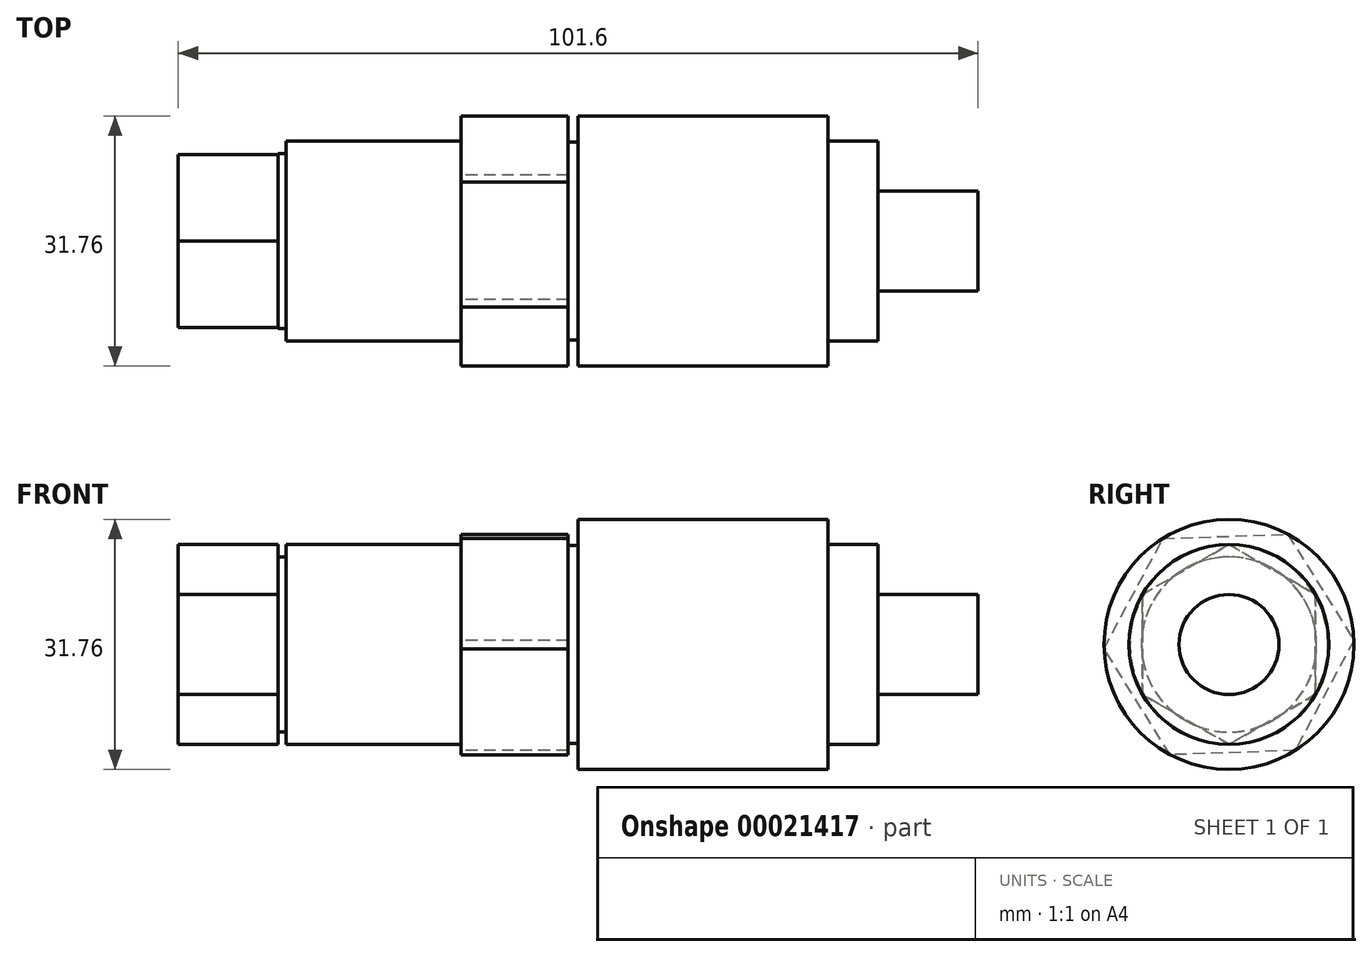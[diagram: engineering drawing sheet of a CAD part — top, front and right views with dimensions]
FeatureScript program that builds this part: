
annotation { "Feature Type Name" : "Feature", "Feature Type Description" : "" }
export const myFeature = defineFeature(function(context is Context, id is Id, definition is map)
    precondition{}
    {
        {
            var Q0;
            Q0=qCreatedBy(makeId("Front.planeOp"),FACE);
            var sketch = newSketch(context, id + "F0", { "sketchPlane" : qUnion([Q0])});
            skLineSegment(sketch, "E0", {"start": v(0, 0) * mm, "end": v(101.6, 0) * mm});
            skLineSegment(sketch, "E1", {"start": v(101.6, 0) * mm, "end": v(101.6, 6.35) * mm});
            skLineSegment(sketch, "E2", {"start": v(101.6, 6.35) * mm, "end": v(88.9, 6.35) * mm});
            skLineSegment(sketch, "E3", {"start": v(88.9, 6.35) * mm, "end": v(88.9, 12.7) * mm});
            skLineSegment(sketch, "E4", {"start": v(88.9, 12.7) * mm, "end": v(82.55, 12.7) * mm});
            skLineSegment(sketch, "E5", {"start": v(82.55, 12.7) * mm, "end": v(82.55, 15.88) * mm});
            skLineSegment(sketch, "E6", {"start": v(82.55, 15.88) * mm, "end": v(50.8, 15.87) * mm});
            skLineSegment(sketch, "E7", {"start": v(50.8, 15.87) * mm, "end": v(50.8, 12.57) * mm});
            skLineSegment(sketch, "E8", {"start": v(50.8, 12.57) * mm, "end": v(49.53, 12.57) * mm});
            skLineSegment(sketch, "E9", {"start": v(49.53, 12.57) * mm, "end": v(49.53, 15.88) * mm});
            skLineSegment(sketch, "E10", {"start": v(49.53, 15.88) * mm, "end": v(35.94, 15.87) * mm});
            skLineSegment(sketch, "E11", {"start": v(35.94, 15.87) * mm, "end": v(35.94, 12.7) * mm});
            skLineSegment(sketch, "E12", {"start": v(35.94, 12.7) * mm, "end": v(13.72, 12.7) * mm});
            skLineSegment(sketch, "E13", {"start": v(13.72, 12.7) * mm, "end": v(13.72, 11.13) * mm});
            skLineSegment(sketch, "E14", {"start": v(13.72, 11.13) * mm, "end": v(12.7, 11.13) * mm});
            skLineSegment(sketch, "E15", {"start": v(12.7, 11.13) * mm, "end": v(12.7, 12.7) * mm});
            skLineSegment(sketch, "E16", {"start": v(12.7, 12.7) * mm, "end": v(0, 12.7) * mm});
            skLineSegment(sketch, "E17", {"start": v(0, 12.7) * mm, "end": v(0, 0) * mm});
            skSolve(sketch);
        }
        {
            var Q0;
            Q0=makeQuery(id+"F0.imprint","IMPRINT",FACE,{"disambiguationData":[TD([[makeQuery(id+"F0.imprint","IMPRINT",EDGE,{"derivedFrom":sQuery(id+"F0.wireOp",EDGE,"E0")}),1.0]])]});
            var Q1;
            Q1=sQuery(id+"F0.wireOp",EDGE,"E0");
            revolve(context, id + "F1", {"entities" : qUnion([Q0]), "axis" : qUnion([Q1]), "revolveType" : RevolveType.FULL});
        }
        {
            var Q0;
            Q0=makeQuery(id+"F1.opRevolve","SWEPT_FACE",FACE,{"disambiguationData":[OSD([sQuery(id+"F0.wireOp",EDGE,"E17")])]});
            var sketch = newSketch(context, id + "F2", { "sketchPlane" : qUnion([Q0])});
            skCircle(sketch, "E18.cCircle", {"center": v(0, 0) * mm, "radius": 12.7 * mm, "construction": true});
            skLineSegment(sketch, "E18.0", {"start": v(0, 12.7) * mm, "end": v(11, 6.35) * mm});
            skLineSegment(sketch, "E18.1", {"start": v(11, 6.35) * mm, "end": v(11, -6.35) * mm});
            skLineSegment(sketch, "E18.2", {"start": v(11, -6.35) * mm, "end": v(0, -12.7) * mm});
            skLineSegment(sketch, "E18.3", {"start": v(0, -12.7) * mm, "end": v(-11, -6.35) * mm});
            skLineSegment(sketch, "E18.4", {"start": v(-11, -6.35) * mm, "end": v(-11, 6.35) * mm});
            skLineSegment(sketch, "E18.5", {"start": v(-11, 6.35) * mm, "end": v(0, 12.7) * mm});
            skSolve(sketch);
        }
        {
            var Q0;
            {var subQ1=sQuery(id+"F2.wireOp",EDGE,"E18.3");Q0=makeQuery(id+"F2.imprint","IMPRINT",FACE,{"disambiguationData":[TD([[makeQuery(id+"F2.imprint","IMPRINT",EDGE,{"derivedFrom":subQ1}),1.0]])]});}
            var Q1;
            {var subQ1=sQuery(id+"F2.wireOp",EDGE,"E18.4");Q1=makeQuery(id+"F2.imprint","IMPRINT",FACE,{"disambiguationData":[TD([[makeQuery(id+"F2.imprint","IMPRINT",EDGE,{"derivedFrom":subQ1}),1.0]])]});}
            var Q2;
            {var subQ1=sQuery(id+"F2.wireOp",EDGE,"E18.5");Q2=makeQuery(id+"F2.imprint","IMPRINT",FACE,{"disambiguationData":[TD([[makeQuery(id+"F2.imprint","IMPRINT",EDGE,{"derivedFrom":subQ1}),1.0]])]});}
            var Q3;
            {var subQ1=sQuery(id+"F2.wireOp",EDGE,"E18.0");Q3=makeQuery(id+"F2.imprint","IMPRINT",FACE,{"disambiguationData":[TD([[makeQuery(id+"F2.imprint","IMPRINT",EDGE,{"derivedFrom":subQ1}),1.0]])]});}
            var Q4;
            {var subQ1=sQuery(id+"F2.wireOp",EDGE,"E18.1");Q4=makeQuery(id+"F2.imprint","IMPRINT",FACE,{"disambiguationData":[TD([[makeQuery(id+"F2.imprint","IMPRINT",EDGE,{"derivedFrom":subQ1}),1.0]])]});}
            var Q5;
            {var subQ1=sQuery(id+"F2.wireOp",EDGE,"E18.2");Q5=makeQuery(id+"F2.imprint","IMPRINT",FACE,{"disambiguationData":[TD([[makeQuery(id+"F2.imprint","IMPRINT",EDGE,{"derivedFrom":subQ1}),1.0]])]});}
            var Q6;
            Q6=makeQuery(id+"F1.opRevolve","SWEPT_FACE",FACE,{"disambiguationData":[OSD([sQuery(id+"F0.wireOp",EDGE,"E15")])]});
            extrude(context, id + "F3", {"entities" : qUnion([Q0, Q1, Q2, Q3, Q4, Q5]), "operationType" : NewBodyOperationType.REMOVE, "endBound" : BoundingType.UP_TO_SURFACE, "oppositeDirection" : true, "endBoundEntityFace" : qUnion([Q6]), "depth" : 25.4 * mm});
        }
        {
            var Q0;
            Q0=makeQuery(id+"F1.opRevolve","SWEPT_FACE",FACE,{"disambiguationData":[OSD([sQuery(id+"F0.wireOp",EDGE,"E11")])]});
            var sketch = newSketch(context, id + "F4", { "sketchPlane" : qUnion([Q0])});
            skCircle(sketch, "E19.cCircle", {"center": v(0, 0) * mm, "radius": 15.88 * mm, "construction": true});
            skLineSegment(sketch, "E19.0", {"start": v(15.87, -0.54) * mm, "end": v(7.46, -14.01) * mm});
            skLineSegment(sketch, "E19.1", {"start": v(7.46, -14.01) * mm, "end": v(-8.4, -13.47) * mm});
            skLineSegment(sketch, "E19.2", {"start": v(-8.4, -13.47) * mm, "end": v(-15.87, 0.54) * mm});
            skLineSegment(sketch, "E19.3", {"start": v(-15.87, 0.54) * mm, "end": v(-7.46, 14.01) * mm});
            skLineSegment(sketch, "E19.4", {"start": v(-7.46, 14.01) * mm, "end": v(8.4, 13.47) * mm});
            skLineSegment(sketch, "E19.5", {"start": v(8.4, 13.47) * mm, "end": v(15.87, -0.54) * mm});
            skSolve(sketch);
        }
        {
            var Q0;
            {var subQ1=sQuery(id+"F4.wireOp",EDGE,"E19.4");Q0=makeQuery(id+"F4.imprint","IMPRINT",FACE,{"disambiguationData":[TD([[makeQuery(id+"F4.imprint","IMPRINT",EDGE,{"derivedFrom":subQ1}),1.0]])]});}
            var Q1;
            {var subQ1=sQuery(id+"F4.wireOp",EDGE,"E19.3");Q1=makeQuery(id+"F4.imprint","IMPRINT",FACE,{"disambiguationData":[TD([[makeQuery(id+"F4.imprint","IMPRINT",EDGE,{"derivedFrom":subQ1}),1.0]])]});}
            var Q2;
            {var subQ1=sQuery(id+"F4.wireOp",EDGE,"E19.2");Q2=makeQuery(id+"F4.imprint","IMPRINT",FACE,{"disambiguationData":[TD([[makeQuery(id+"F4.imprint","IMPRINT",EDGE,{"derivedFrom":subQ1}),1.0]])]});}
            var Q3;
            {var subQ1=sQuery(id+"F4.wireOp",EDGE,"E19.1");Q3=makeQuery(id+"F4.imprint","IMPRINT",FACE,{"disambiguationData":[TD([[makeQuery(id+"F4.imprint","IMPRINT",EDGE,{"derivedFrom":subQ1}),1.0]])]});}
            var Q4;
            {var subQ1=sQuery(id+"F4.wireOp",EDGE,"E19.0");Q4=makeQuery(id+"F4.imprint","IMPRINT",FACE,{"disambiguationData":[TD([[makeQuery(id+"F4.imprint","IMPRINT",EDGE,{"derivedFrom":subQ1}),1.0]])]});}
            var Q5;
            {var subQ1=sQuery(id+"F4.wireOp",EDGE,"E19.5");Q5=makeQuery(id+"F4.imprint","IMPRINT",FACE,{"disambiguationData":[TD([[makeQuery(id+"F4.imprint","IMPRINT",EDGE,{"derivedFrom":subQ1}),1.0]])]});}
            var Q6;
            Q6=makeQuery(id+"F1.opRevolve","SWEPT_FACE",FACE,{"disambiguationData":[OSD([sQuery(id+"F0.wireOp",EDGE,"E9")])]});
            extrude(context, id + "F5", {"entities" : qUnion([Q0, Q1, Q2, Q3, Q4, Q5]), "operationType" : NewBodyOperationType.REMOVE, "endBound" : BoundingType.UP_TO_SURFACE, "oppositeDirection" : true, "endBoundEntityFace" : qUnion([Q6]), "depth" : 25.4 * mm});
        }
    });
